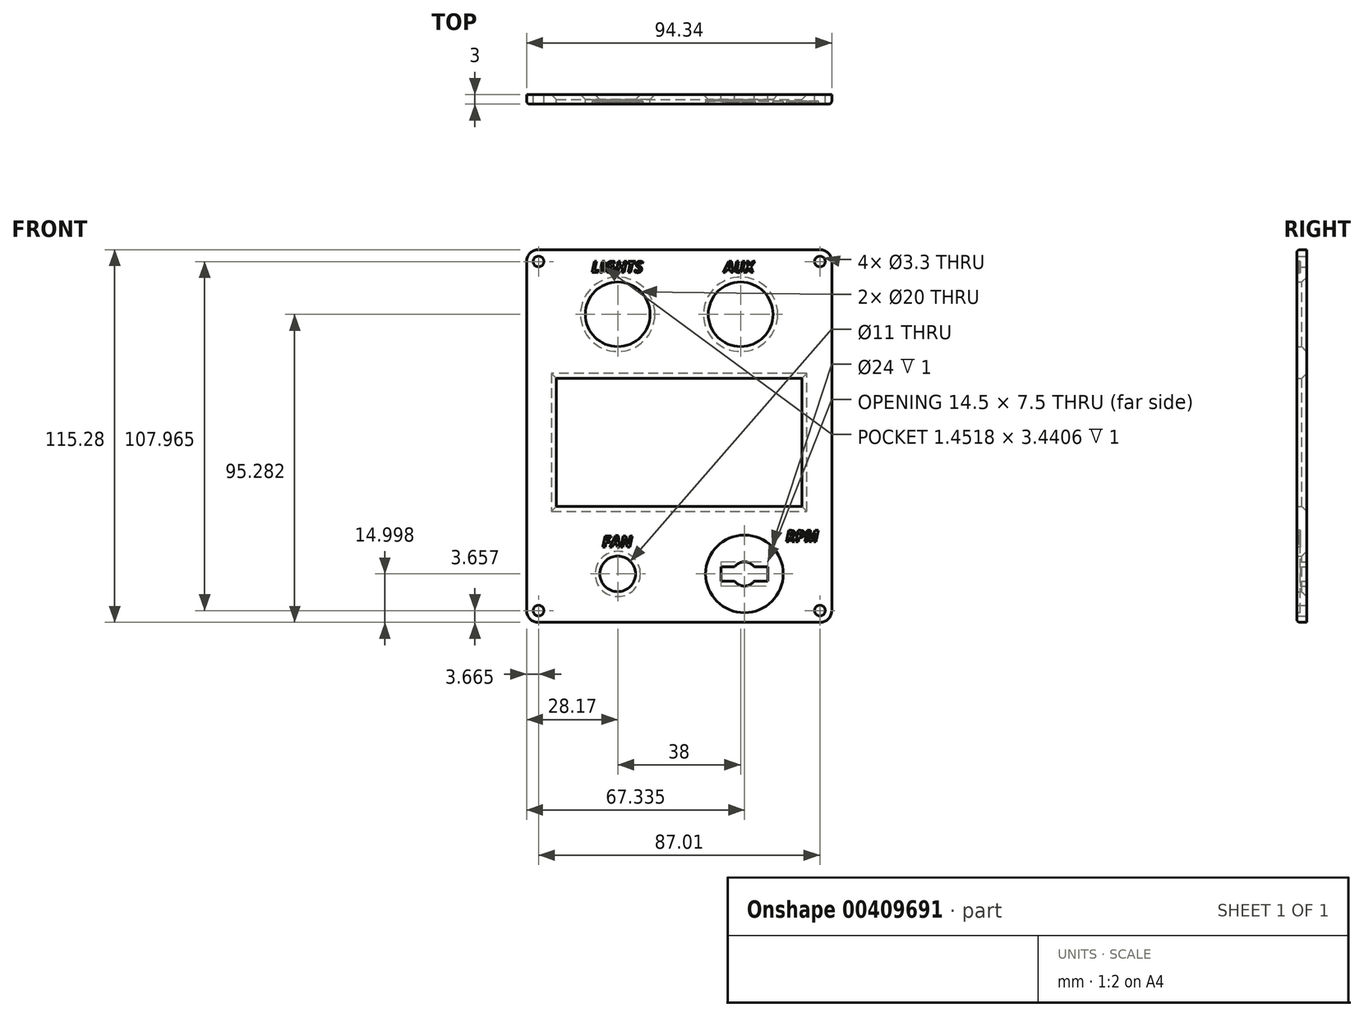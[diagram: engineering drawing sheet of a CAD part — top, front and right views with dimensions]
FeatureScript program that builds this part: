
annotation { "Feature Type Name" : "Feature", "Feature Type Description" : "" }
export const myFeature = defineFeature(function(context is Context, id is Id, definition is map)
    precondition{}
    {
        {
            var Q0;
            Q0=qCreatedBy(makeId("Front.planeOp"),FACE);
            var sketch = newSketch(context, id + "F0", { "sketchPlane" : qUnion([Q0])});
            skLineSegment(sketch, "E0.bottom", {"start": v(43.5, 57.64) * mm, "end": v(-43.5, 57.64) * mm});
            skLineSegment(sketch, "E0.top", {"start": v(43.5, -57.64) * mm, "end": v(-43.5, -57.64) * mm});
            skLineSegment(sketch, "E0.left", {"start": v(47.16, 53.98) * mm, "end": v(47.16, -53.98) * mm});
            skLineSegment(sketch, "E0.right", {"start": v(-47.17, 53.98) * mm, "end": v(-47.16, -53.98) * mm});
            skPoint(sketch, "E0.middle", {"position": v(0, 0) * mm});
            skPoint(sketch, "E1.visualSharp", {"position": v(-47.17, 57.64) * mm});
            skArc(sketch, "E1.filletArc", {"start": v(-43.5, 57.64) * mm, "mid": v(-46.1, 56.57) * mm, "end": v(-47.17, 53.98) * mm});
            skPoint(sketch, "E2.visualSharp", {"position": v(47.16, 57.64) * mm});
            skArc(sketch, "E2.filletArc", {"start": v(47.16, 53.98) * mm, "mid": v(46.1, 56.57) * mm, "end": v(43.5, 57.64) * mm});
            skPoint(sketch, "E3.visualSharp", {"position": v(47.16, -57.64) * mm});
            skArc(sketch, "E3.filletArc", {"start": v(43.5, -57.64) * mm, "mid": v(46.1, -56.57) * mm, "end": v(47.17, -53.98) * mm});
            skPoint(sketch, "E4.visualSharp", {"position": v(-47.16, -57.64) * mm});
            skArc(sketch, "E4.filletArc", {"start": v(-47.16, -53.98) * mm, "mid": v(-46.1, -56.57) * mm, "end": v(-43.5, -57.64) * mm});
            skLineSegment(sketch, "E5.bottom", {"start": v(-37.97, 17.87) * mm, "end": v(37.97, 17.87) * mm});
            skLineSegment(sketch, "E5.top", {"start": v(-37.97, -21.8) * mm, "end": v(37.97, -21.8) * mm});
            skLineSegment(sketch, "E5.left", {"start": v(-37.97, 17.87) * mm, "end": v(-37.97, -21.8) * mm});
            skLineSegment(sketch, "E5.right", {"start": v(37.97, 17.87) * mm, "end": v(37.97, -21.8) * mm});
            skLineSegment(sketch, "E6", {"start": v(0, 57.64) * mm, "end": v(0, -57.64) * mm, "construction": true});
            skLineSegment(sketch, "E7", {"start": v(0, 17.87) * mm, "end": v(0, -21.8) * mm, "construction": true});
            skCircle(sketch, "E8", {"center": v(-19, 37.64) * mm, "radius": 10 * mm});
            skCircle(sketch, "E9", {"center": v(-19, -42.64) * mm, "radius": 5.5 * mm});
            skLineSegment(sketch, "E10.bottom", {"start": v(27.42, -40.4) * mm, "end": v(23.17, -40.4) * mm});
            skLineSegment(sketch, "E10.top", {"start": v(27.42, -44.9) * mm, "end": v(23.17, -44.9) * mm});
            skLineSegment(sketch, "E10.left", {"start": v(27.42, -40.4) * mm, "end": v(27.42, -44.9) * mm});
            skLineSegment(sketch, "E10.right", {"start": v(12.92, -40.4) * mm, "end": v(12.92, -44.9) * mm});
            skPoint(sketch, "E10.middle", {"position": v(20.17, -42.64) * mm});
            skArc(sketch, "E11", {"start": v(17.17, -44.9) * mm, "mid": v(20.17, -46.4) * mm, "end": v(23.17, -44.9) * mm});
            skLineSegment(sketch, "E12.trimOffspring", {"start": v(17.17, -40.4) * mm, "end": v(12.92, -40.4) * mm});
            skLineSegment(sketch, "E13.trimOffspring", {"start": v(17.17, -44.9) * mm, "end": v(12.92, -44.9) * mm});
            skArc(sketch, "E14.trimOffspring", {"start": v(23.17, -40.4) * mm, "mid": v(20.17, -38.9) * mm, "end": v(17.17, -40.4) * mm});
            skCircle(sketch, "E15.MirrorC", {"center": v(19, 37.64) * mm, "radius": 10 * mm});
            skSolve(sketch);
        }
        {
            var Q0;
            Q0=makeQuery(id+"F0.imprint","IMPRINT",FACE,{"disambiguationData":[TD([[makeQuery(id+"F0.imprint","IMPRINT",EDGE,{"derivedFrom":sQuery(id+"F0.wireOp",EDGE,"E0.bottom")}),1.0]])]});
            extrude(context, id + "F1", {"entities" : qUnion([Q0]), "depth" : 3 * mm});
        }
        {
            var Q0;
            Q0=makeQuery(id+"F1.opExtrude","CAP_EDGE",EDGE,{"disambiguationData":[OSD([sQuery(id+"F0.wireOp",EDGE,"E5.bottom")])],"isStart":true});
            var Q1;
            Q1=makeQuery(id+"F1.opExtrude","CAP_EDGE",EDGE,{"disambiguationData":[OSD([sQuery(id+"F0.wireOp",EDGE,"E5.left")])],"isStart":true});
            var Q2;
            Q2=makeQuery(id+"F1.opExtrude","CAP_EDGE",EDGE,{"disambiguationData":[OSD([sQuery(id+"F0.wireOp",EDGE,"E5.top")])],"isStart":true});
            var Q3;
            Q3=makeQuery(id+"F1.opExtrude","CAP_EDGE",EDGE,{"disambiguationData":[OSD([sQuery(id+"F0.wireOp",EDGE,"E5.right")])],"isStart":true});
            var Q4;
            Q4=makeQuery(id+"F1.opExtrude","CAP_EDGE",EDGE,{"disambiguationData":[OSD([sQuery(id+"F0.wireOp",EDGE,"E15.MirrorC")])],"isStart":true});
            var Q5;
            Q5=makeQuery(id+"F1.opExtrude","CAP_EDGE",EDGE,{"disambiguationData":[OSD([sQuery(id+"F0.wireOp",EDGE,"E8")])],"isStart":true});
            var Q6;
            Q6=makeQuery(id+"F1.opExtrude","CAP_EDGE",EDGE,{"disambiguationData":[OSD([sQuery(id+"F0.wireOp",EDGE,"E9")])],"isStart":true});
            chamfer(context, id + "F2", {"entities" : qUnion([Q0, Q1, Q2, Q3, Q4, Q5, Q6]), "width" : 1.5 * mm, "tangentPropagation" : true});
        }
        {
            var Q0;
            Q0=makeQuery(id+"F1.opExtrude","CAP_FACE",FACE,{"disambiguationData":[OSD([sQuery(id+"F0.wireOp",EDGE,"E0.bottom"),sQuery(id+"F0.wireOp",EDGE,"E0.top"),sQuery(id+"F0.wireOp",EDGE,"E0.left"),sQuery(id+"F0.wireOp",EDGE,"E0.right"),sQuery(id+"F0.wireOp",EDGE,"E1.filletArc"),sQuery(id+"F0.wireOp",EDGE,"E2.filletArc"),sQuery(id+"F0.wireOp",EDGE,"E3.filletArc"),sQuery(id+"F0.wireOp",EDGE,"E4.filletArc"),sQuery(id+"F0.wireOp",EDGE,"E5.bottom"),sQuery(id+"F0.wireOp",EDGE,"E5.top"),sQuery(id+"F0.wireOp",EDGE,"E5.left"),sQuery(id+"F0.wireOp",EDGE,"E5.right"),sQuery(id+"F0.wireOp",EDGE,"E8"),sQuery(id+"F0.wireOp",EDGE,"E9"),sQuery(id+"F0.wireOp",EDGE,"E10.bottom"),sQuery(id+"F0.wireOp",EDGE,"E10.top"),sQuery(id+"F0.wireOp",EDGE,"E10.left"),sQuery(id+"F0.wireOp",EDGE,"E10.right"),sQuery(id+"F0.wireOp",EDGE,"E11"),sQuery(id+"F0.wireOp",EDGE,"E12.trimOffspring"),sQuery(id+"F0.wireOp",EDGE,"E13.trimOffspring"),sQuery(id+"F0.wireOp",EDGE,"E14.trimOffspring"),sQuery(id+"F0.wireOp",EDGE,"E15.MirrorC")])],"isStart":false});
            var sketch = newSketch(context, id + "F3", { "sketchPlane" : qUnion([Q0])});
            skCircle(sketch, "E16", {"center": v(20.17, -42.64) * mm, "radius": 12 * mm});
            skSolve(sketch);
        }
        {
            var Q0;
            Q0 = qSketchRegion(id + "F3", true);
            extrude(context, id + "F4", {"entities" : qUnion([Q0]), "operationType" : NewBodyOperationType.REMOVE, "oppositeDirection" : true, "depth" : 1 * mm});
        }
        {
            var Q0;
            Q0=sQuery(id+"F0.wireOp",VERTEX,"E1.filletArc.center");
            var Q1;
            Q1=sQuery(id+"F0.wireOp",VERTEX,"E2.filletArc.center");
            var Q2;
            Q2=sQuery(id+"F0.wireOp",VERTEX,"E4.filletArc.center");
            var Q3;
            Q3=sQuery(id+"F0.wireOp",VERTEX,"E3.filletArc.center");
            var Q4;
            Q4=makeQuery(id+"F1.opExtrude","SWEPT_BODY",BODY,{"disambiguationData":[OSD([sQuery(id+"F0.wireOp",EDGE,"E0.bottom"),sQuery(id+"F0.wireOp",EDGE,"E0.top"),sQuery(id+"F0.wireOp",EDGE,"E0.left"),sQuery(id+"F0.wireOp",EDGE,"E0.right"),sQuery(id+"F0.wireOp",EDGE,"E1.filletArc"),sQuery(id+"F0.wireOp",EDGE,"E2.filletArc"),sQuery(id+"F0.wireOp",EDGE,"E3.filletArc"),sQuery(id+"F0.wireOp",EDGE,"E4.filletArc"),sQuery(id+"F0.wireOp",EDGE,"E5.bottom"),sQuery(id+"F0.wireOp",EDGE,"E5.top"),sQuery(id+"F0.wireOp",EDGE,"E5.left"),sQuery(id+"F0.wireOp",EDGE,"E5.right"),sQuery(id+"F0.wireOp",EDGE,"E8"),sQuery(id+"F0.wireOp",EDGE,"E9"),sQuery(id+"F0.wireOp",EDGE,"E10.bottom"),sQuery(id+"F0.wireOp",EDGE,"E10.top"),sQuery(id+"F0.wireOp",EDGE,"E10.left"),sQuery(id+"F0.wireOp",EDGE,"E10.right"),sQuery(id+"F0.wireOp",EDGE,"E11"),sQuery(id+"F0.wireOp",EDGE,"E12.trimOffspring"),sQuery(id+"F0.wireOp",EDGE,"E13.trimOffspring"),sQuery(id+"F0.wireOp",EDGE,"E14.trimOffspring"),sQuery(id+"F0.wireOp",EDGE,"E15.MirrorC")])]});
            hole(context, id + "F5", {"style" : HoleStyle.SIMPLE, "endStyle" : HoleEndStyle.THROUGH, "oppositeDirection" : true, "standardTappedOrClearance" : lookupTablePath({ "standard" : "ISO", "fit" : "Normal", "size" : "M3", "type" : "Clearance" }), "standardBlindInLast" : lookupTablePath({ "fit" : "Standard", "standard" : "ISO", "size" : "M3", "type" : "Clearance" }), "holeDiameter" : 3.3 * mm, "isTappedThrough" : true, "tappedDepth" : 12 * mm, "tapClearance" : 3, "startFromSketch" : true, "locations" : qUnion([Q0, Q1, Q2, Q3]), "scope" : qUnion([Q4])});
        }
        {
            var Q0;
            Q0=makeQuery(id+"F1.opExtrude","CAP_EDGE",EDGE,{"disambiguationData":[OSD([sQuery(id+"F0.wireOp",EDGE,"E0.top")])],"isStart":false});
            var Q1;
            Q1=makeQuery(id+"F1.opExtrude","CAP_EDGE",EDGE,{"disambiguationData":[OSD([sQuery(id+"F0.wireOp",EDGE,"E4.filletArc")])],"isStart":false});
            var Q2;
            Q2=makeQuery(id+"F1.opExtrude","CAP_EDGE",EDGE,{"disambiguationData":[OSD([sQuery(id+"F0.wireOp",EDGE,"E0.right")])],"isStart":false});
            var Q3;
            Q3=makeQuery(id+"F1.opExtrude","CAP_EDGE",EDGE,{"disambiguationData":[OSD([sQuery(id+"F0.wireOp",EDGE,"E1.filletArc")])],"isStart":false});
            var Q4;
            Q4=makeQuery(id+"F1.opExtrude","CAP_EDGE",EDGE,{"disambiguationData":[OSD([sQuery(id+"F0.wireOp",EDGE,"E0.bottom")])],"isStart":false});
            var Q5;
            Q5=makeQuery(id+"F1.opExtrude","CAP_EDGE",EDGE,{"disambiguationData":[OSD([sQuery(id+"F0.wireOp",EDGE,"E2.filletArc")])],"isStart":false});
            var Q6;
            Q6=makeQuery(id+"F1.opExtrude","CAP_EDGE",EDGE,{"disambiguationData":[OSD([sQuery(id+"F0.wireOp",EDGE,"E0.left")])],"isStart":false});
            var Q7;
            Q7=makeQuery(id+"F1.opExtrude","CAP_EDGE",EDGE,{"disambiguationData":[OSD([sQuery(id+"F0.wireOp",EDGE,"E3.filletArc")])],"isStart":false});
            fillet(context, id + "F6", {"entities" : qUnion([Q0, Q1, Q2, Q3, Q4, Q5, Q6, Q7]), "radius" : 1 * mm, "tangentPropagation" : true, "allowEdgeOverflow" : false});
        }
        {
            var Q0;
            Q0=makeQuery(id+"F1.opExtrude","CAP_FACE",FACE,{"disambiguationData":[OSD([sQuery(id+"F0.wireOp",EDGE,"E0.bottom"),sQuery(id+"F0.wireOp",EDGE,"E0.top"),sQuery(id+"F0.wireOp",EDGE,"E0.left"),sQuery(id+"F0.wireOp",EDGE,"E0.right"),sQuery(id+"F0.wireOp",EDGE,"E1.filletArc"),sQuery(id+"F0.wireOp",EDGE,"E2.filletArc"),sQuery(id+"F0.wireOp",EDGE,"E3.filletArc"),sQuery(id+"F0.wireOp",EDGE,"E4.filletArc"),sQuery(id+"F0.wireOp",EDGE,"E5.bottom"),sQuery(id+"F0.wireOp",EDGE,"E5.top"),sQuery(id+"F0.wireOp",EDGE,"E5.left"),sQuery(id+"F0.wireOp",EDGE,"E5.right"),sQuery(id+"F0.wireOp",EDGE,"E8"),sQuery(id+"F0.wireOp",EDGE,"E9"),sQuery(id+"F0.wireOp",EDGE,"E10.bottom"),sQuery(id+"F0.wireOp",EDGE,"E10.top"),sQuery(id+"F0.wireOp",EDGE,"E10.left"),sQuery(id+"F0.wireOp",EDGE,"E10.right"),sQuery(id+"F0.wireOp",EDGE,"E11"),sQuery(id+"F0.wireOp",EDGE,"E12.trimOffspring"),sQuery(id+"F0.wireOp",EDGE,"E13.trimOffspring"),sQuery(id+"F0.wireOp",EDGE,"E14.trimOffspring"),sQuery(id+"F0.wireOp",EDGE,"E15.MirrorC")])],"isStart":false});
            var sketch = newSketch(context, id + "F7", { "sketchPlane" : qUnion([Q0])});
            skText(sketch, "E17", { "text": "LIGHTS", "fontName": "OpenSans-BoldItalic.ttf"});
            skText(sketch, "E18", { "text": "AUX", "fontName": "OpenSans-BoldItalic.ttf"});
            skText(sketch, "E19", { "text": "FAN", "fontName": "OpenSans-BoldItalic.ttf"});
            skText(sketch, "E20", { "text": "RPM", "fontName": "OpenSans-BoldItalic.ttf"});
            const initialGuessF7  = {"E17": [-0.0271, 0.0506, 1, 0, 0.00347], "E18": [0.01388, 0.0506, 1, 0, 0.00347], "E19": [-0.02378, -0.0343, 1, 0, 0.00347], "E20": [0.03303, -0.03264, 1, 0, 0.00347]};
            skSetInitialGuess(sketch, initialGuessF7);
            skSolve(sketch);
        }
        {
            var Q0;
            Q0 = qSketchRegion(id + "F7", true);
            extrude(context, id + "F8", {"entities" : qUnion([Q0]), "operationType" : NewBodyOperationType.REMOVE, "oppositeDirection" : true, "depth" : 1 * mm});
        }
    });
